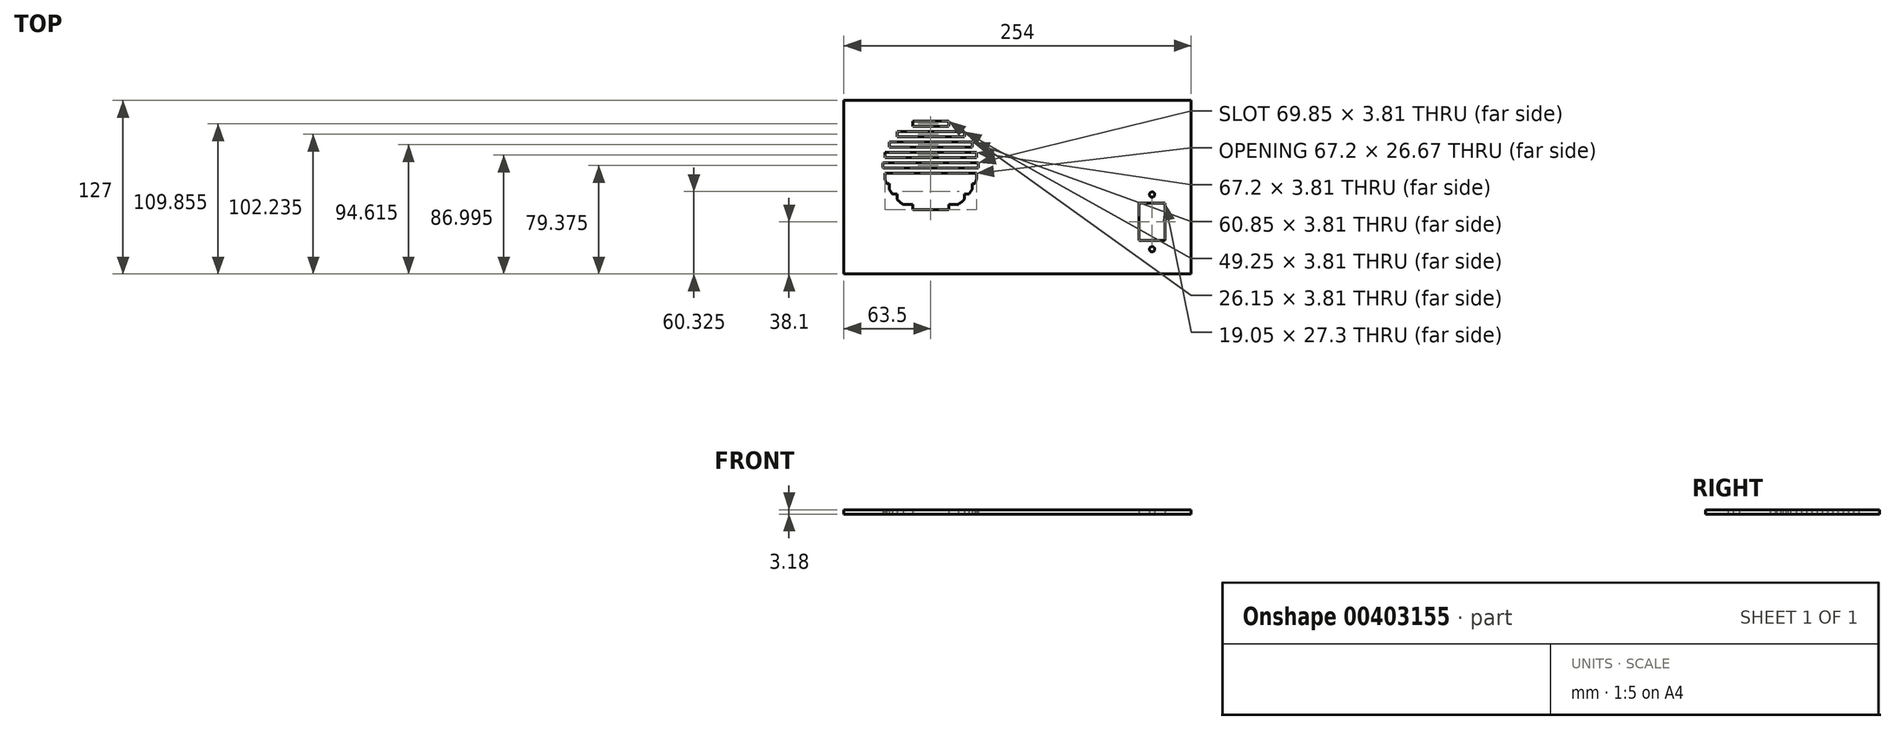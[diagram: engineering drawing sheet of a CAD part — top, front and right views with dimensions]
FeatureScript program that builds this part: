
annotation { "Feature Type Name" : "Feature", "Feature Type Description" : "" }
export const myFeature = defineFeature(function(context is Context, id is Id, definition is map)
    precondition{}
    {
        {
            var Q0;
            Q0=qCreatedBy(makeId("Top.planeOp"),FACE);
            var sketch = newSketch(context, id + "F0", { "sketchPlane" : qUnion([Q0])});
            skLineSegment(sketch, "E0.bottom", {"start": v(127, -50.8) * mm, "end": v(-127, -50.8) * mm});
            skLineSegment(sketch, "E0.top", {"start": v(127, 76.2) * mm, "end": v(-127, 76.2) * mm});
            skLineSegment(sketch, "E0.left", {"start": v(127, -50.8) * mm, "end": v(127, 76.2) * mm});
            skLineSegment(sketch, "E0.right", {"start": v(-127, -50.8) * mm, "end": v(-127, 76.2) * mm});
            skPoint(sketch, "E0.middle", {"position": v(0, 12.7) * mm});
            skLineSegment(sketch, "E1.bottom", {"start": v(107.94, -26.35) * mm, "end": v(88.9, -26.35) * mm});
            skLineSegment(sketch, "E1.top", {"start": v(107.94, 0.95) * mm, "end": v(88.9, 0.95) * mm});
            skLineSegment(sketch, "E1.left", {"start": v(107.94, -26.35) * mm, "end": v(107.94, 0.95) * mm});
            skLineSegment(sketch, "E1.right", {"start": v(88.9, -26.35) * mm, "end": v(88.9, 0.95) * mm});
            skPoint(sketch, "E1.middle", {"position": v(98.42, -12.7) * mm});
            skLineSegment(sketch, "E2", {"start": v(98.42, -32.7) * mm, "end": v(98.42, 7.3) * mm});
            skPoint(sketch, "E2.startSnap0", {"position": v(98.42, -26.35) * mm});
            skPoint(sketch, "E2.endSnap0", {"position": v(98.42, 0.95) * mm});
            skCircle(sketch, "E3", {"center": v(98.42, 7.3) * mm, "radius": 1.9 * mm});
            skCircle(sketch, "E4", {"center": v(98.42, -32.7) * mm, "radius": 1.9 * mm});
            skCircle(sketch, "E5", {"center": v(-63.5, 28.58) * mm, "radius": 34.93 * mm});
            skLineSegment(sketch, "E6.bottom", {"start": v(-98.37, 30.48) * mm, "end": v(-28.63, 30.48) * mm});
            skLineSegment(sketch, "E6.top", {"start": v(-98.37, 26.67) * mm, "end": v(-28.63, 26.67) * mm});
            skLineSegment(sketch, "E6.left", {"start": v(-98.37, 30.48) * mm, "end": v(-98.37, 26.67) * mm});
            skLineSegment(sketch, "E6.right", {"start": v(-28.63, 30.48) * mm, "end": v(-28.63, 26.67) * mm});
            skLineSegment(sketch, "E7", {"start": v(-68.79, 28.58) * mm, "end": v(-58.77, 28.58) * mm});
            skLineSegment(sketch, "E8", {"start": v(-97.95, 34.3) * mm, "end": v(-29.05, 34.3) * mm});
            skLineSegment(sketch, "E9", {"start": v(-97.1, 38.1) * mm, "end": v(-29.9, 38.1) * mm});
            skLineSegment(sketch, "E10", {"start": v(-95.78, 41.91) * mm, "end": v(-31.22, 41.91) * mm});
            skLineSegment(sketch, "E11", {"start": v(-93.93, 45.72) * mm, "end": v(-33.07, 45.72) * mm});
            skLineSegment(sketch, "E12", {"start": v(-91.44, 49.53) * mm, "end": v(-35.56, 49.53) * mm});
            skLineSegment(sketch, "E13", {"start": v(-88.13, 53.34) * mm, "end": v(-38.87, 53.34) * mm});
            skLineSegment(sketch, "E14", {"start": v(-83.58, 57.15) * mm, "end": v(-43.42, 57.15) * mm});
            skLineSegment(sketch, "E15", {"start": v(-76.58, 60.96) * mm, "end": v(-50.42, 60.96) * mm});
            skLineSegment(sketch, "E16.MirrorCS", {"start": v(-97.95, 22.86) * mm, "end": v(-29.05, 22.86) * mm});
            skLineSegment(sketch, "E17.MirrorCS", {"start": v(-97.1, 19.05) * mm, "end": v(-29.9, 19.05) * mm});
            skLineSegment(sketch, "E18.MirrorCS", {"start": v(-95.78, 15.24) * mm, "end": v(-31.22, 15.24) * mm});
            skLineSegment(sketch, "E19.MirrorCS", {"start": v(-93.93, 11.43) * mm, "end": v(-33.07, 11.43) * mm});
            skLineSegment(sketch, "E20.MirrorCS", {"start": v(-91.44, 7.62) * mm, "end": v(-35.56, 7.62) * mm});
            skLineSegment(sketch, "E21.MirrorCS", {"start": v(-88.13, 3.81) * mm, "end": v(-38.87, 3.81) * mm});
            skLineSegment(sketch, "E22.MirrorCS", {"start": v(-83.58, 0) * mm, "end": v(-43.42, 0) * mm});
            skLineSegment(sketch, "E23.MirrorCS", {"start": v(-76.58, -3.81) * mm, "end": v(-50.42, -3.81) * mm});
            skLineSegment(sketch, "E24.top", {"start": v(-97.1, 34.3) * mm, "end": v(-29.9, 34.3) * mm});
            skLineSegment(sketch, "E24.left", {"start": v(-97.1, 38.1) * mm, "end": v(-97.1, 34.3) * mm});
            skLineSegment(sketch, "E24.right", {"start": v(-29.9, 38.1) * mm, "end": v(-29.9, 34.3) * mm});
            skLineSegment(sketch, "E25.top", {"start": v(-93.93, 41.91) * mm, "end": v(-33.07, 41.91) * mm});
            skLineSegment(sketch, "E25.left", {"start": v(-93.93, 45.72) * mm, "end": v(-93.93, 41.91) * mm});
            skLineSegment(sketch, "E25.right", {"start": v(-33.07, 45.72) * mm, "end": v(-33.07, 41.91) * mm});
            skLineSegment(sketch, "E26.top", {"start": v(-88.13, 49.53) * mm, "end": v(-38.87, 49.53) * mm});
            skLineSegment(sketch, "E26.left", {"start": v(-88.13, 53.34) * mm, "end": v(-88.13, 49.53) * mm});
            skLineSegment(sketch, "E26.right", {"start": v(-38.87, 53.34) * mm, "end": v(-38.87, 49.53) * mm});
            skLineSegment(sketch, "E27.top", {"start": v(-76.58, 57.15) * mm, "end": v(-50.42, 57.15) * mm});
            skLineSegment(sketch, "E27.left", {"start": v(-76.58, 60.96) * mm, "end": v(-76.58, 57.15) * mm});
            skLineSegment(sketch, "E27.right", {"start": v(-50.42, 60.96) * mm, "end": v(-50.42, 57.15) * mm});
            skLineSegment(sketch, "E28.top", {"start": v(-76.58, 0) * mm, "end": v(-50.42, 0) * mm});
            skLineSegment(sketch, "E28.left", {"start": v(-76.58, -3.81) * mm, "end": v(-76.58, 0) * mm});
            skLineSegment(sketch, "E28.right", {"start": v(-50.42, -3.81) * mm, "end": v(-50.42, 0) * mm});
            skLineSegment(sketch, "E29.top", {"start": v(-88.13, 7.62) * mm, "end": v(-38.87, 7.62) * mm});
            skLineSegment(sketch, "E29.left", {"start": v(-88.13, 3.8) * mm, "end": v(-88.13, 7.62) * mm});
            skLineSegment(sketch, "E29.right", {"start": v(-38.87, 3.8) * mm, "end": v(-38.87, 7.62) * mm});
            skLineSegment(sketch, "E30.top", {"start": v(-93.93, 15.24) * mm, "end": v(-33.07, 15.24) * mm});
            skLineSegment(sketch, "E30.left", {"start": v(-93.93, 11.43) * mm, "end": v(-93.93, 15.24) * mm});
            skLineSegment(sketch, "E30.right", {"start": v(-33.07, 11.43) * mm, "end": v(-33.07, 15.24) * mm});
            skLineSegment(sketch, "E31.top", {"start": v(-97.1, 22.86) * mm, "end": v(-29.9, 22.86) * mm});
            skLineSegment(sketch, "E31.left", {"start": v(-97.1, 19.05) * mm, "end": v(-97.1, 22.86) * mm});
            skLineSegment(sketch, "E31.right", {"start": v(-29.9, 19.05) * mm, "end": v(-29.9, 22.86) * mm});
            skSolve(sketch);
        }
        {
            var Q0;
            Q0=makeQuery(id+"F0.imprint","IMPRINT",FACE,{"disambiguationData":[TD([[makeQuery(id+"F0.imprint","IMPRINT",EDGE,{"derivedFrom":sQuery(id+"F0.wireOp",EDGE,"E0.bottom")}),-1.0]])]});
            var Q1;
            {var subQ0=sQuery(id+"F0.wireOp",EDGE,"E23.MirrorCS");Q1=makeQuery(id+"F0.imprint","IMPRINT",FACE,{"disambiguationData":[TD([[makeQuery(id+"F0.imprint","IMPRINT",EDGE,{"derivedFrom":subQ0}),-1.0]])]});}
            var Q2;
            {var subQ3=sQuery(id+"F0.wireOp",EDGE,"E28.top");Q2=makeQuery(id+"F0.imprint","IMPRINT",FACE,{"disambiguationData":[TD([[makeQuery(id+"F0.imprint","IMPRINT",EDGE,{"derivedFrom":subQ3}),1.0]])]});}
            var Q3;
            {var subQ3=sQuery(id+"F0.wireOp",EDGE,"E28.right");Q3=makeQuery(id+"F0.imprint","IMPRINT",FACE,{"disambiguationData":[TD([[makeQuery(id+"F0.imprint","IMPRINT",EDGE,{"derivedFrom":subQ3}),-1.0]])]});}
            var Q4;
            {var subQ3=sQuery(id+"F0.wireOp",EDGE,"E28.left");Q4=makeQuery(id+"F0.imprint","IMPRINT",FACE,{"disambiguationData":[TD([[makeQuery(id+"F0.imprint","IMPRINT",EDGE,{"derivedFrom":subQ3}),1.0]])]});}
            var Q5;
            {var subQ3=sQuery(id+"F0.wireOp",EDGE,"E29.left");Q5=makeQuery(id+"F0.imprint","IMPRINT",FACE,{"disambiguationData":[TD([[makeQuery(id+"F0.imprint","IMPRINT",EDGE,{"derivedFrom":subQ3}),1.0]])]});}
            var Q6;
            {var subQ3=sQuery(id+"F0.wireOp",EDGE,"E29.right");Q6=makeQuery(id+"F0.imprint","IMPRINT",FACE,{"disambiguationData":[TD([[makeQuery(id+"F0.imprint","IMPRINT",EDGE,{"derivedFrom":subQ3}),-1.0]])]});}
            var Q7;
            {var subQ3=sQuery(id+"F0.wireOp",EDGE,"E29.top");Q7=makeQuery(id+"F0.imprint","IMPRINT",FACE,{"disambiguationData":[TD([[makeQuery(id+"F0.imprint","IMPRINT",EDGE,{"derivedFrom":subQ3}),1.0]])]});}
            var Q8;
            {var subQ3=sQuery(id+"F0.wireOp",EDGE,"E30.top");Q8=makeQuery(id+"F0.imprint","IMPRINT",FACE,{"disambiguationData":[TD([[makeQuery(id+"F0.imprint","IMPRINT",EDGE,{"derivedFrom":subQ3}),1.0]])]});}
            var Q9;
            {var subQ3=sQuery(id+"F0.wireOp",EDGE,"E30.right");Q9=makeQuery(id+"F0.imprint","IMPRINT",FACE,{"disambiguationData":[TD([[makeQuery(id+"F0.imprint","IMPRINT",EDGE,{"derivedFrom":subQ3}),-1.0]])]});}
            var Q10;
            {var subQ3=sQuery(id+"F0.wireOp",EDGE,"E30.left");Q10=makeQuery(id+"F0.imprint","IMPRINT",FACE,{"disambiguationData":[TD([[makeQuery(id+"F0.imprint","IMPRINT",EDGE,{"derivedFrom":subQ3}),1.0]])]});}
            var Q11;
            {var subQ3=sQuery(id+"F0.wireOp",EDGE,"E31.right");Q11=makeQuery(id+"F0.imprint","IMPRINT",FACE,{"disambiguationData":[TD([[makeQuery(id+"F0.imprint","IMPRINT",EDGE,{"derivedFrom":subQ3}),-1.0]])]});}
            var Q12;
            {var subQ3=sQuery(id+"F0.wireOp",EDGE,"E31.left");Q12=makeQuery(id+"F0.imprint","IMPRINT",FACE,{"disambiguationData":[TD([[makeQuery(id+"F0.imprint","IMPRINT",EDGE,{"derivedFrom":subQ3}),1.0]])]});}
            var Q13;
            {var subQ4=sQuery(id+"F0.wireOp",EDGE,"E6.top");Q13=makeQuery(id+"F0.imprint","IMPRINT",FACE,{"disambiguationData":[TD([[makeQuery(id+"F0.imprint","IMPRINT",EDGE,{"derivedFrom":subQ4}),-1.0]])]});}
            var Q14;
            {var subQ5=sQuery(id+"F0.wireOp",EDGE,"E6.bottom");Q14=makeQuery(id+"F0.imprint","IMPRINT",FACE,{"disambiguationData":[TD([[makeQuery(id+"F0.imprint","IMPRINT",EDGE,{"derivedFrom":subQ5}),1.0]])]});}
            var Q15;
            {var subQ3=sQuery(id+"F0.wireOp",EDGE,"E24.right");Q15=makeQuery(id+"F0.imprint","IMPRINT",FACE,{"disambiguationData":[TD([[makeQuery(id+"F0.imprint","IMPRINT",EDGE,{"derivedFrom":subQ3}),1.0]])]});}
            var Q16;
            {var subQ3=sQuery(id+"F0.wireOp",EDGE,"E24.left");Q16=makeQuery(id+"F0.imprint","IMPRINT",FACE,{"disambiguationData":[TD([[makeQuery(id+"F0.imprint","IMPRINT",EDGE,{"derivedFrom":subQ3}),-1.0]])]});}
            var Q17;
            {var subQ5=sQuery(id+"F0.wireOp",EDGE,"E9");Q17=makeQuery(id+"F0.imprint","IMPRINT",FACE,{"disambiguationData":[TD([[makeQuery(id+"F0.imprint","IMPRINT",EDGE,{"derivedFrom":subQ5}),1.0]])]});}
            var Q18;
            {var subQ3=sQuery(id+"F0.wireOp",EDGE,"E25.right");Q18=makeQuery(id+"F0.imprint","IMPRINT",FACE,{"disambiguationData":[TD([[makeQuery(id+"F0.imprint","IMPRINT",EDGE,{"derivedFrom":subQ3}),1.0]])]});}
            var Q19;
            {var subQ3=sQuery(id+"F0.wireOp",EDGE,"E25.left");Q19=makeQuery(id+"F0.imprint","IMPRINT",FACE,{"disambiguationData":[TD([[makeQuery(id+"F0.imprint","IMPRINT",EDGE,{"derivedFrom":subQ3}),-1.0]])]});}
            var Q20;
            {var subQ5=sQuery(id+"F0.wireOp",EDGE,"E11");Q20=makeQuery(id+"F0.imprint","IMPRINT",FACE,{"disambiguationData":[TD([[makeQuery(id+"F0.imprint","IMPRINT",EDGE,{"derivedFrom":subQ5}),1.0]])]});}
            var Q21;
            {var subQ3=sQuery(id+"F0.wireOp",EDGE,"E26.right");Q21=makeQuery(id+"F0.imprint","IMPRINT",FACE,{"disambiguationData":[TD([[makeQuery(id+"F0.imprint","IMPRINT",EDGE,{"derivedFrom":subQ3}),1.0]])]});}
            var Q22;
            {var subQ3=sQuery(id+"F0.wireOp",EDGE,"E26.left");Q22=makeQuery(id+"F0.imprint","IMPRINT",FACE,{"disambiguationData":[TD([[makeQuery(id+"F0.imprint","IMPRINT",EDGE,{"derivedFrom":subQ3}),-1.0]])]});}
            var Q23;
            {var subQ5=sQuery(id+"F0.wireOp",EDGE,"E13");Q23=makeQuery(id+"F0.imprint","IMPRINT",FACE,{"disambiguationData":[TD([[makeQuery(id+"F0.imprint","IMPRINT",EDGE,{"derivedFrom":subQ5}),1.0]])]});}
            var Q24;
            {var subQ3=sQuery(id+"F0.wireOp",EDGE,"E27.right");Q24=makeQuery(id+"F0.imprint","IMPRINT",FACE,{"disambiguationData":[TD([[makeQuery(id+"F0.imprint","IMPRINT",EDGE,{"derivedFrom":subQ3}),1.0]])]});}
            var Q25;
            {var subQ3=sQuery(id+"F0.wireOp",EDGE,"E27.left");Q25=makeQuery(id+"F0.imprint","IMPRINT",FACE,{"disambiguationData":[TD([[makeQuery(id+"F0.imprint","IMPRINT",EDGE,{"derivedFrom":subQ3}),-1.0]])]});}
            var Q26;
            {var subQ0=sQuery(id+"F0.wireOp",EDGE,"E15");Q26=makeQuery(id+"F0.imprint","IMPRINT",FACE,{"disambiguationData":[TD([[makeQuery(id+"F0.imprint","IMPRINT",EDGE,{"derivedFrom":subQ0}),1.0]])]});}
            extrude(context, id + "F1", {"entities" : qUnion([Q0, Q1, Q2, Q3, Q4, Q5, Q6, Q7, Q8, Q9, Q10, Q11, Q12, Q13, Q14, Q15, Q16, Q17, Q18, Q19, Q20, Q21, Q22, Q23, Q24, Q25, Q26]), "depth" : 3.17 * mm});
        }
    });
